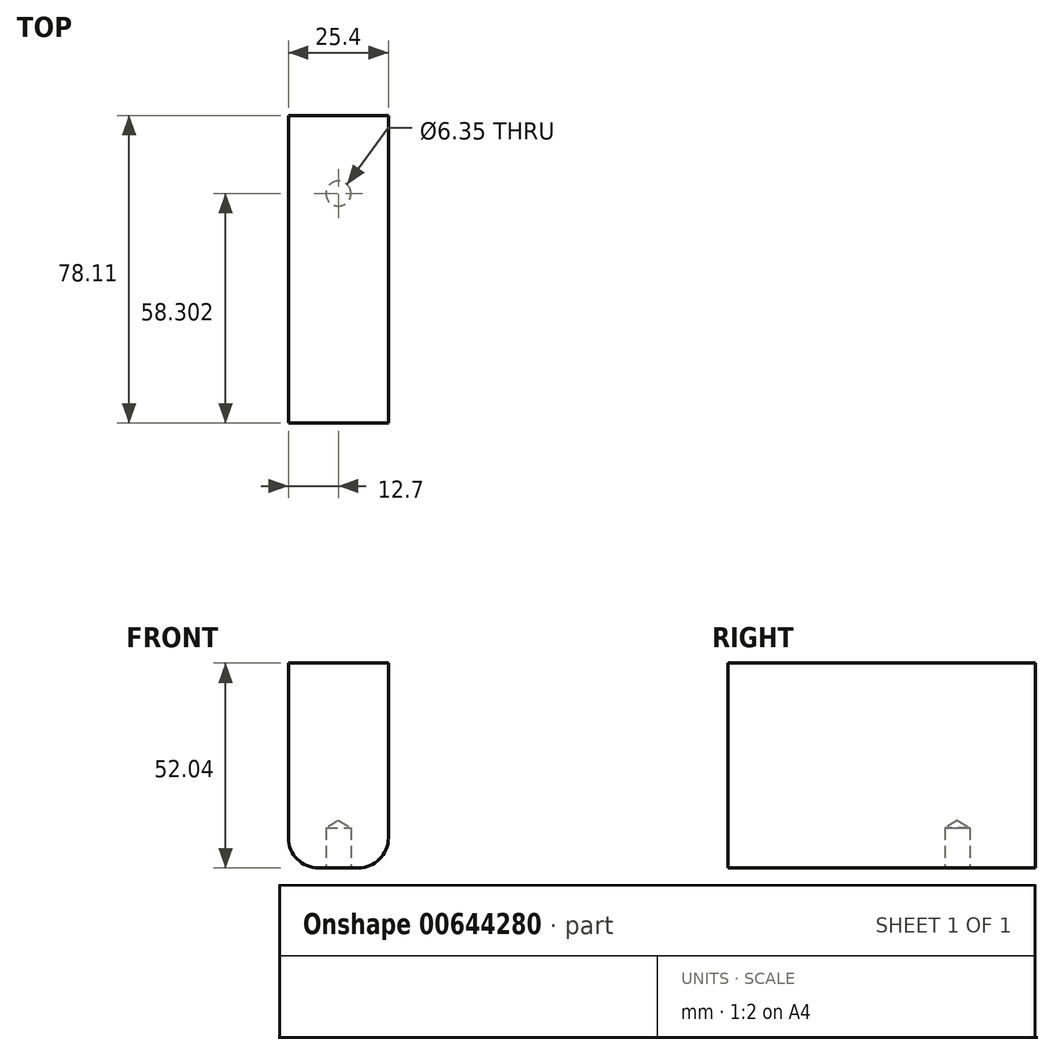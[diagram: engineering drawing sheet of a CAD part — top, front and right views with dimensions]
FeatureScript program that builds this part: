
annotation { "Feature Type Name" : "Feature", "Feature Type Description" : "" }
export const myFeature = defineFeature(function(context is Context, id is Id, definition is map)
    precondition{}
    {
        {
            var Q0;
            Q0=qCreatedBy(makeId("Right.planeOp"),FACE);
            var sketch = newSketch(context, id + "F0", { "sketchPlane" : qUnion([Q0])});
            skLineSegment(sketch, "E0.bottom", {"start": v(-21.52, 0) * mm, "end": v(56.6, 0) * mm});
            skLineSegment(sketch, "E0.top", {"start": v(-21.52, 52.04) * mm, "end": v(56.6, 52.04) * mm});
            skLineSegment(sketch, "E0.left", {"start": v(-21.52, 0) * mm, "end": v(-21.52, 52.04) * mm});
            skLineSegment(sketch, "E0.right", {"start": v(56.6, 0) * mm, "end": v(56.6, 52.04) * mm});
            skSolve(sketch);
        }
        {
            var Q0;
            Q0 = qSketchRegion(id + "F0", true);
            extrude(context, id + "F1", {"entities" : qUnion([Q0]), "depth" : 25.4 * mm, "offsetDistance" : 25.4 * mm});
        }
        {
            var Q0;
            Q0=makeQuery(id+"F1.opExtrude","CAP_EDGE",EDGE,{"disambiguationData":[OSD([sQuery(id+"F0.wireOp",EDGE,"E0.bottom")])],"isStart":true});
            fillet(context, id + "F2", {"entities" : qUnion([Q0]), "radius" : 7.62 * mm, "tangentPropagation" : true, "allowEdgeOverflow" : false});
        }
        {
            var Q0;
            Q0=makeQuery(id+"F1.opExtrude","CAP_EDGE",EDGE,{"disambiguationData":[OSD([sQuery(id+"F0.wireOp",EDGE,"E0.bottom")])],"isStart":false});
            fillet(context, id + "F3", {"entities" : qUnion([Q0]), "radius" : 7.62 * mm, "tangentPropagation" : true, "allowEdgeOverflow" : false});
        }
        {
            var Q0;
            Q0=makeQuery(id+"F1.opExtrude","SWEPT_FACE",FACE,{"disambiguationData":[OSD([sQuery(id+"F0.wireOp",EDGE,"E0.bottom")])]});
            var sketch = newSketch(context, id + "F4", { "sketchPlane" : qUnion([Q0])});
            skCircle(sketch, "E1", {"center": v(12.7, -36.78) * mm, "radius": 3.16 * mm});
            skPoint(sketch, "E1.centerSnap0", {"position": v(12.7, -56.6) * mm});
            skSolve(sketch);
        }
        {
            var Q0;
            Q0=sQuery(id+"F4.wireOp",VERTEX,"E1.center");
            var Q1;
            Q1=makeQuery(id+"F1.opExtrude","SWEPT_BODY",BODY,{"disambiguationData":[OSD([sQuery(id+"F0.wireOp",EDGE,"E0.bottom"),sQuery(id+"F0.wireOp",EDGE,"E0.top"),sQuery(id+"F0.wireOp",EDGE,"E0.left"),sQuery(id+"F0.wireOp",EDGE,"E0.right")])]});
            hole(context, id + "F5", {"style" : HoleStyle.SIMPLE, "endStyle" : HoleEndStyle.BLIND, "holeDiameter" : 6.35 * mm, "majorDiameter" : 6.35 * mm, "holeDepth" : 10.16 * mm, "isTappedThrough" : true, "tappedDepth" : 12.7 * mm, "tapClearance" : 3, "locations" : qUnion([Q0]), "scope" : qUnion([Q1])});
        }
    });
